# Revit family: Domotics-DomesticRanges-GEWISS-27COMBI_SYSTEM-IP40_2P+2P+2P_4P+4P+4P_VERTICAL
name_source: partatom
category: Apparecchi elettrici
revit_build: Autodesk Revit 2016 (Build: 20161004_0715(x64)
units: mm (PartAtom-declared; Revit-internal decimal feet)

## family parameters
Condiviso = No
Host = Superficie
Mantenere orientamento annotazione = Sì
Numero OmniClass = 23.80.30.14.24
Punto di calcolo locali = No
Quota connettore circolare = Usa diametro
Taglio con vuoti quando caricato = Sì
Tipo di parte = Normale
Titolo OmniClass = Junction Boxes

## types (1)
- Domotics-DomesticRanges-GEWISS-27COMBI_SYSTEM-IP40_2P+2P+2P_4P+4P+4P_VERTICAL
    Bidimensionale = bidimensionale system contenitori IP40 3PV : 4P
    Catalogue = DOMOTICS
    Catalogue Range = 27COMBI
    Characteristics = Halogen free
    Colour = Grey RAL 7035
    Compartment pre-arrangement = 3
    Configuration = Module 4 x 3
    Description: = 12 gang
    Descrizione = VERT.12(4X3) GANG ENCLOSURE IP40
    Dimensions LxHxD (mm) = 132x198x55
    EAN code = 8011564055353
    Electrocod = 0212
    Glow Wire Test = 650°C
    IDF = 5774814a-3d43-4596-b29a-0fe0abd6822c
    IDT = 3d13f3d9-1d3d-499b-bc30-5f792185b541
    IP degree = IP40
    Immagine tipo = GW27024.jpg
    Installation temperature = -25 +60 °C
    Insulation class = II
    Larghezza scatola = 132 mm  [stored 0.433071 ft]
    Lid screws = Corrosion-resistant steel
    Modello = GW27024
    No. knockout holes Ã˜ 23 = 12
    No. knockout holes Ã˜23 = 12 on sides / 3 on the bottom
    Outer dim. LxHxD (mm) = 132x198x55
    Produttore = GEWISS S.p.A.
    Prospetto di default = 1219 mm
    SCATOLA = GEWISS GRIGIO
    SEO = Enclosure
    Shock resistance = IK07
    Standard; = EN 60670-1
    Technical sheet = https://www.gewiss.com
    Thermo-pressure with ball = 70
    Tipo = SYSTEM CONTENITORI IP40 3P V_BASE : GW27024 - 4x3 posti verticali
    Torque screws tightening = 0,8NM
    Type of knockout holes = Removable with tool
    URL = https://www.gewiss.com
    Version file RFA = 19.4

note: source unit labels omitted for Thermo-pressure with ball — the stored unit's dimension contradicts the parameter name (converter mislabeling)

note: [stored X ft] marks values corroborated as IEEE doubles in the binary element streams (Revit-internal decimal feet)

## geometry (parser evidence)
native form markers: Blend x2
no freeform markers — native parametric forms only
